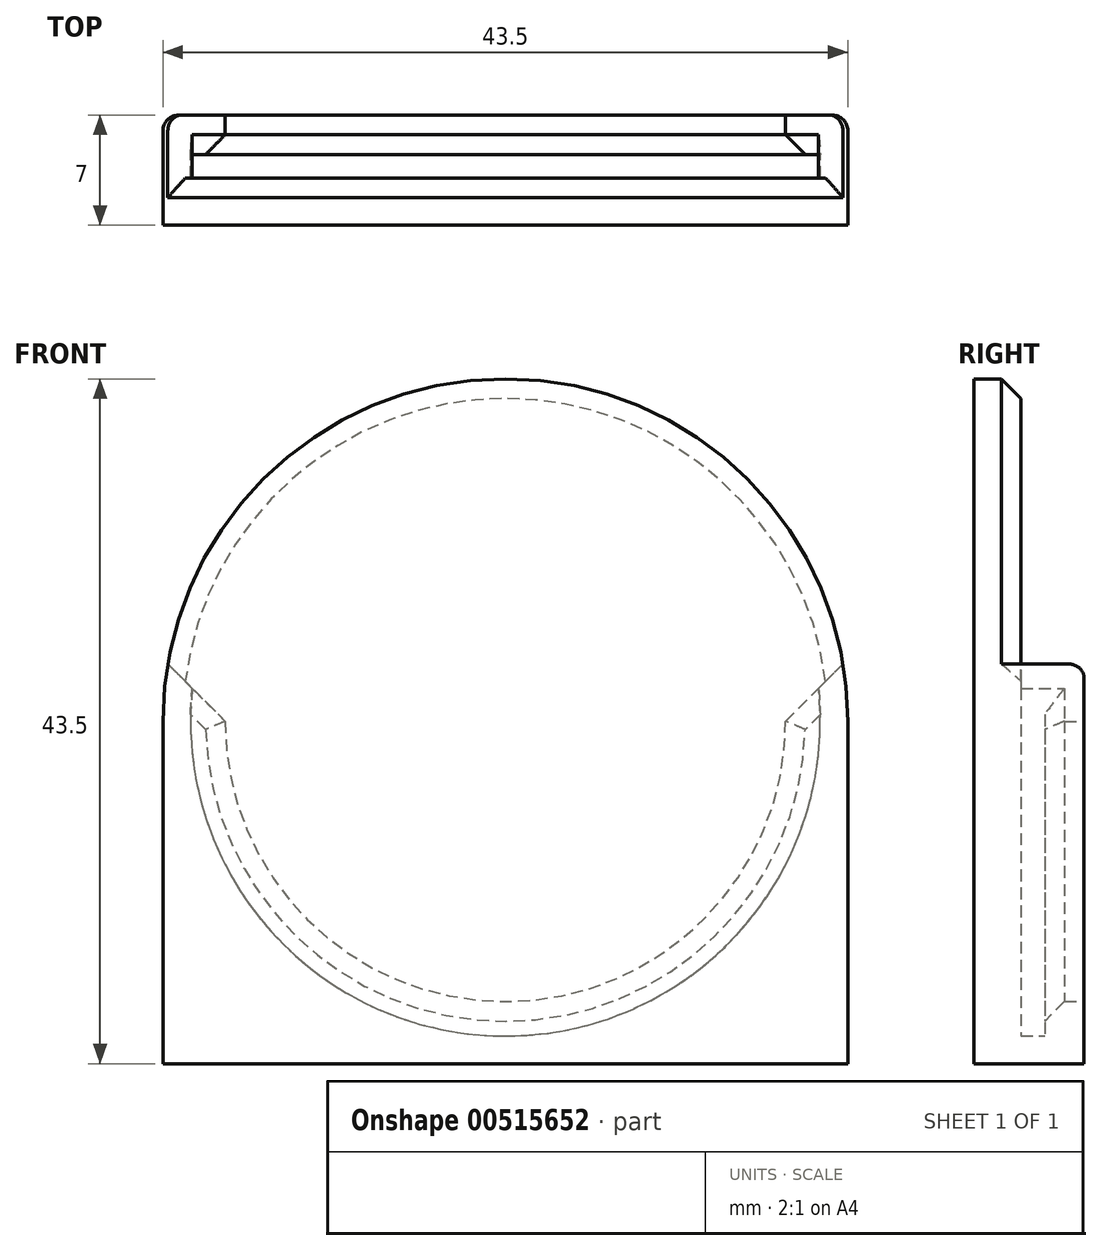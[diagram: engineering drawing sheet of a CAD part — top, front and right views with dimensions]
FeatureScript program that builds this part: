
annotation { "Feature Type Name" : "Feature", "Feature Type Description" : "" }
export const myFeature = defineFeature(function(context is Context, id is Id, definition is map)
    precondition{}
    {
        {
            var Q0;
            Q0=qCreatedBy(makeId("Front.planeOp"),FACE);
            var sketch = newSketch(context, id + "F0", { "sketchPlane" : qUnion([Q0])});
            skArc(sketch, "E0", {"start": v(-17.8, 0) * mm, "mid": v(0, -17.8) * mm, "end": v(17.8, 0) * mm});
            skArc(sketch, "E1", {"start": v(-21.44, 3.64) * mm, "mid": v(0, -21.75) * mm, "end": v(21.44, 3.64) * mm});
            skLineSegment(sketch, "E2", {"start": v(-21.44, 3.64) * mm, "end": v(-17.8, 0) * mm});
            skLineSegment(sketch, "E3", {"start": v(17.8, 0) * mm, "end": v(21.44, 3.64) * mm});
            skSolve(sketch);
        }
        {
            var Q0;
            Q0=makeQuery(id+"F0.imprint","IMPRINT",FACE,{"disambiguationData":[TD([[makeQuery(id+"F0.imprint","IMPRINT",EDGE,{"derivedFrom":sQuery(id+"F0.wireOp",EDGE,"E0")}),-1.0]])]});
            extrude(context, id + "F1", {"entities" : qUnion([Q0]), "depth" : 2.5 * mm, "offsetDistance" : 25 * mm});
        }
        {
            var Q0;
            Q0=makeQuery(id+"F1.opExtrude","CAP_FACE",FACE,{"disambiguationData":[OSD([sQuery(id+"F0.wireOp",EDGE,"E0"),sQuery(id+"F0.wireOp",EDGE,"E1"),sQuery(id+"F0.wireOp",EDGE,"E2"),sQuery(id+"F0.wireOp",EDGE,"E3")])],"isStart":false});
            var sketch = newSketch(context, id + "F2", { "sketchPlane" : qUnion([Q0])});
            skCircle(sketch, "E4", {"center": v(0, 0) * mm, "radius": 21.75 * mm});
            skCircle(sketch, "E5", {"center": v(0, 0) * mm, "radius": 20 * mm});
            skSolve(sketch);
        }
        {
            var Q0;
            {var subQ0=sQuery(id+"F2.wireOp",EDGE,"E4");var subQ1=makeQuery(id+"F1.opExtrude","CAP_EDGE",EDGE,{"disambiguationData":[OSD([sQuery(id+"F0.wireOp",EDGE,"E2")])],"isStart":false});var subQ2=makeQuery(id+"F2.imprint","INTERSECT",VERTEX,{"derivedFrom":[subQ1,subQ0]});Q0=makeQuery(id+"F2.imprint","IMPRINT",FACE,{"disambiguationData":[TD([[makeQuery(id+"F2.imprint","IMPRINT",EDGE,{"disambiguationData":[TD([[subQ2,-1.0]])],"derivedFrom":subQ0}),1.0]])]});}
            extrude(context, id + "F3", {"entities" : qUnion([Q0]), "operationType" : NewBodyOperationType.ADD, "depth" : 1.5 * mm, "offsetDistance" : 25 * mm});
        }
        {
            var Q0;
            Q0=makeQuery(id+"F3.opExtrude","CAP_FACE",FACE,{"disambiguationData":[OSD([sQuery(id+"F0.wireOp",EDGE,"E2"),sQuery(id+"F0.wireOp",EDGE,"E3"),sQuery(id+"F2.wireOp",EDGE,"E4"),sQuery(id+"F2.wireOp",EDGE,"E5")])],"isStart":false});
            var sketch = newSketch(context, id + "F4", { "sketchPlane" : qUnion([Q0])});
            skCircle(sketch, "E6", {"center": v(0, 0) * mm, "radius": 21.75 * mm});
            skSolve(sketch);
        }
        {
            var Q0;
            Q0=makeQuery(id+"F4.imprint","IMPRINT",FACE,{"disambiguationData":[TD([[makeQuery(id+"F4.imprint","IMPRINT",EDGE,{"derivedFrom":makeQuery(id+"F3.opExtrude","CAP_EDGE",EDGE,{"disambiguationData":[OSD([sQuery(id+"F2.wireOp",EDGE,"E5")])],"isStart":false})}),1.0]])]});
            var Q1;
            Q1=makeQuery(id+"F4.imprint","IMPRINT",FACE,{"disambiguationData":[TD([[makeQuery(id+"F4.imprint","IMPRINT",EDGE,{"derivedFrom":makeQuery(id+"F3.opExtrude","CAP_EDGE",EDGE,{"disambiguationData":[OSD([sQuery(id+"F2.wireOp",EDGE,"E5")])],"isStart":false})}),-1.0]])]});
            extrude(context, id + "F5", {"entities" : qUnion([Q0, Q1]), "operationType" : NewBodyOperationType.ADD, "depth" : 3 * mm, "offsetDistance" : 25 * mm});
        }
        {
            var Q0;
            Q0=makeQuery(id+"F5.opExtrude","CAP_FACE",FACE,{"disambiguationData":[OSD([sQuery(id+"F4.wireOp",EDGE,"E6")])],"isStart":false});
            var sketch = newSketch(context, id + "F6", { "sketchPlane" : qUnion([Q0])});
            skLineSegment(sketch, "E7.bottom", {"start": v(-21.75, 0) * mm, "end": v(21.75, 0) * mm});
            skLineSegment(sketch, "E7.top", {"start": v(-21.75, -21.75) * mm, "end": v(21.75, -21.75) * mm});
            skLineSegment(sketch, "E7.left", {"start": v(-21.75, 0) * mm, "end": v(-21.75, -21.75) * mm});
            skLineSegment(sketch, "E7.right", {"start": v(21.75, 0) * mm, "end": v(21.75, -21.75) * mm});
            skSolve(sketch);
        }
        {
            var Q0;
            {var subQ0=sQuery(id+"F6.wireOp",EDGE,"E7.left");Q0=makeQuery(id+"F6.imprint","IMPRINT",FACE,{"disambiguationData":[TD([[makeQuery(id+"F6.imprint","IMPRINT",EDGE,{"derivedFrom":subQ0}),1.0]])]});}
            var Q1;
            {var subQ0=sQuery(id+"F6.wireOp",EDGE,"E7.right");Q1=makeQuery(id+"F6.imprint","IMPRINT",FACE,{"disambiguationData":[TD([[makeQuery(id+"F6.imprint","IMPRINT",EDGE,{"derivedFrom":subQ0}),-1.0]])]});}
            var Q2;
            Q2=makeQuery(id+"F1.opExtrude","CAP_FACE",FACE,{"disambiguationData":[OSD([sQuery(id+"F0.wireOp",EDGE,"E0"),sQuery(id+"F0.wireOp",EDGE,"E1"),sQuery(id+"F0.wireOp",EDGE,"E2"),sQuery(id+"F0.wireOp",EDGE,"E3")])],"isStart":true});
            extrude(context, id + "F7", {"entities" : qUnion([Q0, Q1]), "operationType" : NewBodyOperationType.ADD, "endBound" : BoundingType.UP_TO_SURFACE, "oppositeDirection" : true, "depth" : 25 * mm, "endBoundEntityFace" : qUnion([Q2]), "offsetDistance" : 25 * mm});
        }
        {
            var Q0;
            Q0=makeQuery(id+"F5.opExtrude","CAP_EDGE",EDGE,{"disambiguationData":[OSD([sQuery(id+"F4.wireOp",EDGE,"E6")])],"isStart":true});
            var Q1;
            Q1=makeQuery(id+"F1.opExtrude","CAP_EDGE",EDGE,{"disambiguationData":[OSD([sQuery(id+"F0.wireOp",EDGE,"E3")])],"isStart":false});
            var Q2;
            Q2=makeQuery(id+"F1.opExtrude","CAP_EDGE",EDGE,{"disambiguationData":[OSD([sQuery(id+"F0.wireOp",EDGE,"E0")])],"isStart":false});
            var Q3;
            Q3=makeQuery(id+"F1.opExtrude","CAP_EDGE",EDGE,{"disambiguationData":[OSD([sQuery(id+"F0.wireOp",EDGE,"E2")])],"isStart":false});
            chamfer(context, id + "F8", {"entities" : qUnion([Q0, Q1, Q2, Q3]), "width" : 1.25 * mm, "tangentPropagation" : true});
        }
        {
            var Q0;
            Q0=makeQuery(id+"F7.opExtrude","CAP_EDGE",EDGE,{"disambiguationData":[OSD([sQuery(id+"F6.wireOp",EDGE,"E7.right")])],"isStart":false});
            var Q1;
            Q1=makeQuery(id+"F7.opExtrude","CAP_EDGE",EDGE,{"disambiguationData":[OSD([sQuery(id+"F6.wireOp",EDGE,"E7.left")])],"isStart":false});
            fillet(context, id + "F9", {"entities" : qUnion([Q0, Q1]), "radius" : 1 * mm, "tangentPropagation" : true, "allowEdgeOverflow" : false});
        }
    });
